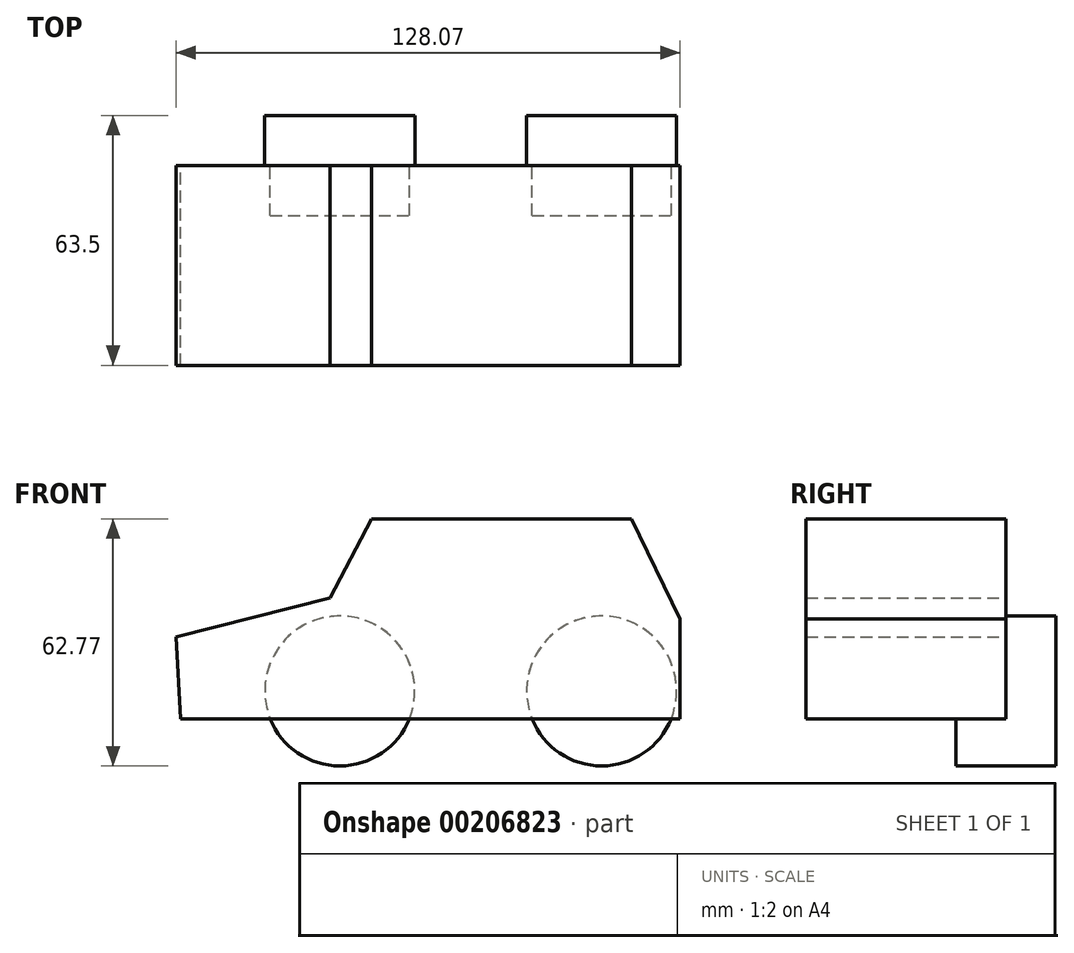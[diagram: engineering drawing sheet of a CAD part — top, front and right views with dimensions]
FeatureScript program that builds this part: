
annotation { "Feature Type Name" : "Feature", "Feature Type Description" : "" }
export const myFeature = defineFeature(function(context is Context, id is Id, definition is map)
    precondition{}
    {
        {
            var Q0;
            Q0=qCreatedBy(makeId("Front.planeOp"),FACE);
            var sketch = newSketch(context, id + "F0", { "sketchPlane" : qUnion([Q0])});
            skLineSegment(sketch, "E0.top", {"start": v(-44.45, -25.4) * mm, "end": v(44.45, -25.4) * mm});
            skLineSegment(sketch, "E0.right", {"start": v(44.45, 25.4) * mm, "end": v(44.45, 25.4) * mm});
            skPoint(sketch, "E0.middle", {"position": v(0, 0) * mm});
            skLineSegment(sketch, "E1", {"start": v(-44.45, 5.3) * mm, "end": v(-83.62, -4.58) * mm});
            skLineSegment(sketch, "E2", {"start": v(-44.45, -25.4) * mm, "end": v(-82.42, -25.4) * mm});
            skLineSegment(sketch, "E3", {"start": v(-82.42, -25.4) * mm, "end": v(-83.62, -4.58) * mm});
            skLineSegment(sketch, "E4", {"start": v(-44.45, 5.3) * mm, "end": v(-33.98, 25.4) * mm});
            skLineSegment(sketch, "E5", {"start": v(-33.98, 25.4) * mm, "end": v(32.04, 25.4) * mm});
            skLineSegment(sketch, "E6", {"start": v(-44.45, 25.4) * mm, "end": v(-44.45, 25.23) * mm});
            skLineSegment(sketch, "E7", {"start": v(-44.45, 5.3) * mm, "end": v(-44.45, 5.3) * mm});
            skLineSegment(sketch, "E8", {"start": v(-44.45, 25.23) * mm, "end": v(-44.45, 25.06) * mm});
            skLineSegment(sketch, "E9", {"start": v(-44.45, 5.3) * mm, "end": v(-44.45, -25.4) * mm});
            skLineSegment(sketch, "E10", {"start": v(24.1, 25.4) * mm, "end": v(24.1, 25.4) * mm});
            skLineSegment(sketch, "E11", {"start": v(44.45, 0) * mm, "end": v(44.45, -25.4) * mm});
            skLineSegment(sketch, "E12", {"start": v(44.45, 0) * mm, "end": v(32.04, 25.4) * mm});
            skSolve(sketch);
        }
        {
            var Q0;
            Q0=makeQuery(id+"F0.imprint","IMPRINT",FACE,{"disambiguationData":[TD([[makeQuery(id+"F0.imprint","IMPRINT",EDGE,{"derivedFrom":sQuery(id+"F0.wireOp",EDGE,"E0.top")}),1.0]])]});
            var Q1;
            Q1=makeQuery(id+"F0.imprint","IMPRINT",FACE,{"disambiguationData":[TD([[makeQuery(id+"F0.imprint","IMPRINT",EDGE,{"derivedFrom":sQuery(id+"F0.wireOp",EDGE,"E1")}),1.0]])]});
            extrude(context, id + "F1", {"entities" : qUnion([Q0, Q1]), "depth" : 50.8 * mm});
        }
        {
            var Q0;
            Q0=qCreatedBy(makeId("Front.planeOp"),FACE);
            var sketch = newSketch(context, id + "F2", { "sketchPlane" : qUnion([Q0])});
            skCircle(sketch, "E13", {"center": v(24.48, -18.32) * mm, "radius": 19.05 * mm});
            skLineSegment(sketch, "E14", {"start": v(24.48, -18.32) * mm, "end": v(-42.03, -18.32) * mm});
            skCircle(sketch, "E15", {"center": v(-42.03, -18.32) * mm, "radius": 19.05 * mm});
            skSolve(sketch);
        }
        {
            var Q0;
            Q0=makeQuery(id+"F2.imprint","IMPRINT",FACE,{"disambiguationData":[TD([[makeQuery(id+"F2.imprint","IMPRINT",EDGE,{"derivedFrom":sQuery(id+"F2.wireOp",EDGE,"E15")}),1.0]])]});
            var Q1;
            Q1=makeQuery(id+"F2.imprint","IMPRINT",FACE,{"disambiguationData":[TD([[makeQuery(id+"F2.imprint","IMPRINT",EDGE,{"derivedFrom":sQuery(id+"F2.wireOp",EDGE,"E13")}),1.0]])]});
            extrude(context, id + "F3", {"entities" : qUnion([Q0, Q1]), "operationType" : NewBodyOperationType.REMOVE, "depth" : 12.7 * mm});
        }
        {
            var Q0;
            Q0=makeQuery(id+"F2.imprint","IMPRINT",FACE,{"disambiguationData":[TD([[makeQuery(id+"F2.imprint","IMPRINT",EDGE,{"derivedFrom":sQuery(id+"F2.wireOp",EDGE,"E13")}),1.0]])]});
            var Q1;
            Q1=makeQuery(id+"F2.imprint","IMPRINT",FACE,{"disambiguationData":[TD([[makeQuery(id+"F2.imprint","IMPRINT",EDGE,{"derivedFrom":sQuery(id+"F2.wireOp",EDGE,"E15")}),1.0]])]});
            extrude(context, id + "F4", {"entities" : qUnion([Q0, Q1]), "depth" : 12.7 * mm});
        }
        {
            var Q0;
            Q0=makeQuery(id+"F4.opExtrude","SWEPT_BODY",BODY,{"disambiguationData":[OSD([sQuery(id+"F2.wireOp",EDGE,"E15")])]});
            var Q1;
            Q1=makeQuery(id+"F4.opExtrude","SWEPT_BODY",BODY,{"disambiguationData":[OSD([sQuery(id+"F2.wireOp",EDGE,"E13")])]});
            var Q2;
            Q2=qCreatedBy(makeId("Front.planeOp"),FACE);
            mirror(context, id + "F5", {"operationType" : NewBodyOperationType.ADD, "entities" : qUnion([Q0, Q1]), "mirrorPlane" : qUnion([Q2])});
        }
    });
